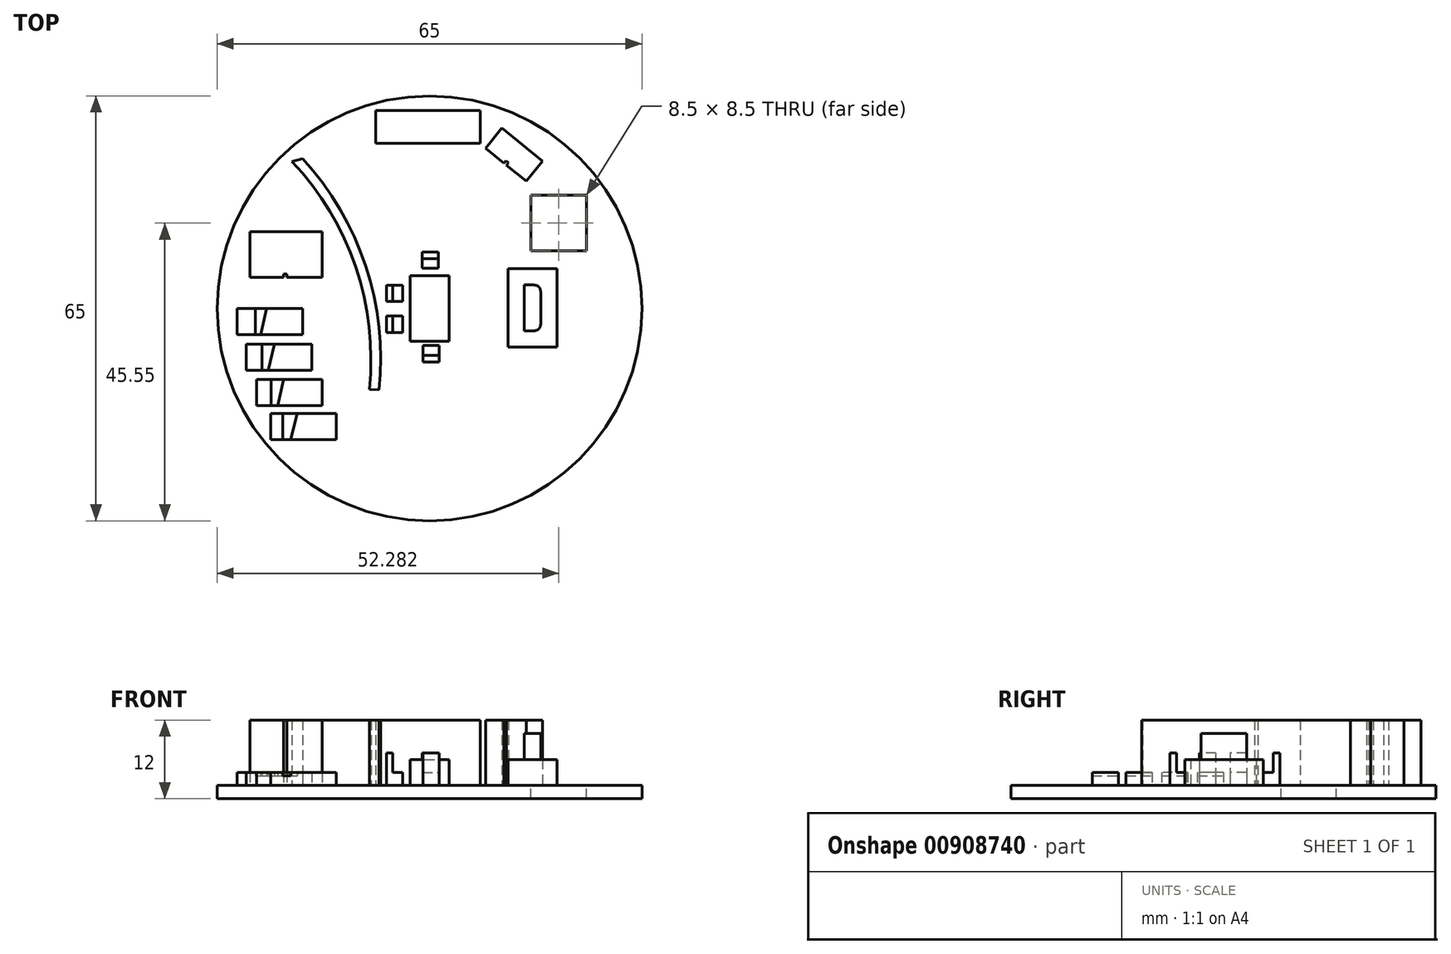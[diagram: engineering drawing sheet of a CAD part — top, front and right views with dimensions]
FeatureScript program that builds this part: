
annotation { "Feature Type Name" : "Feature", "Feature Type Description" : "" }
export const myFeature = defineFeature(function(context is Context, id is Id, definition is map)
    precondition{}
    {
        {
            var Q0;
            Q0=qCreatedBy(makeId("Top.planeOp"),FACE);
            var sketch = newSketch(context, id + "F0", { "sketchPlane" : qUnion([Q0])});
            skCircle(sketch, "E0", {"center": v(0, 0) * mm, "radius": 32.5 * mm});
            skSolve(sketch);
        }
        {
            var Q0;
            Q0=qSketchRegion(id+"F0",true);
            extrude(context, id + "F1", {"entities" : qUnion([Q0]), "depth" : 2 * mm, "offsetDistance" : 25 * mm});
        }
        {
            var Q0;
            Q0=makeQuery(id+"F1.opExtrude","CAP_FACE",FACE,{"disambiguationData":[OSD([sQuery(id+"F0.wireOp",EDGE,"E0")])],"isStart":false});
            var sketch = newSketch(context, id + "F2", { "sketchPlane" : qUnion([Q0])});
            skLineSegment(sketch, "E1.bottom", {"start": v(-8.27, 30.26) * mm, "end": v(7.73, 30.26) * mm});
            skLineSegment(sketch, "E1.top", {"start": v(-8.27, 25.26) * mm, "end": v(7.73, 25.26) * mm});
            skLineSegment(sketch, "E1.left", {"start": v(-8.27, 30.26) * mm, "end": v(-8.27, 25.26) * mm});
            skLineSegment(sketch, "E1.right", {"start": v(7.73, 30.26) * mm, "end": v(7.73, 25.26) * mm});
            skLineSegment(sketch, "E2.bottom", {"start": v(11.09, 27.6) * mm, "end": v(8.57, 24.5) * mm});
            skLineSegment(sketch, "E2.top", {"start": v(17.3, 22.56) * mm, "end": v(14.78, 19.46) * mm});
            skLineSegment(sketch, "E2.left", {"start": v(11.09, 27.6) * mm, "end": v(17.3, 22.56) * mm});
            skLineSegment(sketch, "E2.right", {"start": v(8.57, 24.5) * mm, "end": v(11.38, 22.21) * mm});
            skLineSegment(sketch, "E3.bottom", {"start": v(-27.46, 11.75) * mm, "end": v(-16.46, 11.75) * mm});
            skLineSegment(sketch, "E3.top", {"start": v(-27.46, 4.75) * mm, "end": v(-22.33, 4.75) * mm});
            skLineSegment(sketch, "E3.left", {"start": v(-27.46, 11.75) * mm, "end": v(-27.46, 4.75) * mm});
            skLineSegment(sketch, "E3.right", {"start": v(-16.46, 11.75) * mm, "end": v(-16.46, 4.75) * mm});
            skLineSegment(sketch, "E4", {"start": v(11.38, 22.21) * mm, "end": v(11.7, 22.6) * mm});
            skLineSegment(sketch, "E5", {"start": v(11.7, 22.6) * mm, "end": v(12.09, 22.28) * mm});
            skLineSegment(sketch, "E6", {"start": v(12.09, 22.28) * mm, "end": v(11.77, 21.9) * mm});
            skLineSegment(sketch, "E7.trimOffspring", {"start": v(11.77, 21.9) * mm, "end": v(14.78, 19.46) * mm});
            skArc(sketch, "E8", {"start": v(-7.72, -12.48) * mm, "mid": v(-9.77, 6.46) * mm, "end": v(-19.4, 22.9) * mm});
            skArc(sketch, "E9.0", {"start": v(-9.21, -12.36) * mm, "mid": v(-11.31, 6.36) * mm, "end": v(-21.05, 22.49) * mm});
            skLineSegment(sketch, "E10", {"start": v(-21.05, 22.49) * mm, "end": v(-19.4, 22.9) * mm});
            skLineSegment(sketch, "E11", {"start": v(-9.21, -12.36) * mm, "end": v(-7.72, -12.48) * mm});
            skLineSegment(sketch, "E12", {"start": v(-21.83, 4.75) * mm, "end": v(-21.83, 5.25) * mm});
            skLineSegment(sketch, "E13", {"start": v(-21.83, 5.25) * mm, "end": v(-22.33, 5.25) * mm});
            skLineSegment(sketch, "E14", {"start": v(-22.33, 5.25) * mm, "end": v(-22.33, 4.75) * mm});
            skLineSegment(sketch, "E15.trimOffspring", {"start": v(-21.83, 4.75) * mm, "end": v(-16.46, 4.75) * mm});
            skSolve(sketch);
        }
        {
            var Q0;
            Q0 = qSketchRegion(id + "F2", true);
            extrude(context, id + "F3", {"entities" : qUnion([Q0]), "operationType" : NewBodyOperationType.ADD, "depth" : 10 * mm, "offsetDistance" : 25 * mm});
        }
        {
            var Q0;
            Q0=makeQuery(id+"F1.opExtrude","CAP_FACE",FACE,{"disambiguationData":[OSD([sQuery(id+"F0.wireOp",EDGE,"E0")])],"isStart":false});
            var sketch = newSketch(context, id + "F4", { "sketchPlane" : qUnion([Q0])});
            skLineSegment(sketch, "E16.bottom", {"start": v(-3, 5) * mm, "end": v(3, 5) * mm});
            skLineSegment(sketch, "E16.top", {"start": v(-3, -5) * mm, "end": v(3, -5) * mm});
            skLineSegment(sketch, "E16.left", {"start": v(-3, 5) * mm, "end": v(-3, -5) * mm});
            skLineSegment(sketch, "E16.right", {"start": v(3, 5) * mm, "end": v(3, -5) * mm});
            skLineSegment(sketch, "E17.bottom", {"start": v(12, 6.08) * mm, "end": v(19.5, 6.08) * mm});
            skLineSegment(sketch, "E17.top", {"start": v(12, -5.92) * mm, "end": v(19.5, -5.92) * mm});
            skLineSegment(sketch, "E17.left", {"start": v(12, 6.08) * mm, "end": v(12, -5.92) * mm});
            skLineSegment(sketch, "E17.right", {"start": v(19.5, 6.08) * mm, "end": v(19.5, -5.92) * mm});
            skSolve(sketch);
        }
        {
            var Q0;
            Q0 = qSketchRegion(id + "F4", true);
            extrude(context, id + "F5", {"entities" : qUnion([Q0]), "operationType" : NewBodyOperationType.ADD, "depth" : 4 * mm, "offsetDistance" : 25 * mm});
        }
        {
            var Q0;
            Q0=makeQuery(id+"F5.opExtrude","CAP_FACE",FACE,{"disambiguationData":[OSD([sQuery(id+"F4.wireOp",EDGE,"E17.bottom"),sQuery(id+"F4.wireOp",EDGE,"E17.top"),sQuery(id+"F4.wireOp",EDGE,"E17.left"),sQuery(id+"F4.wireOp",EDGE,"E17.right")])],"isStart":false});
            var sketch = newSketch(context, id + "F6", { "sketchPlane" : qUnion([Q0])});
            skLineSegment(sketch, "E18.0", {"start": v(14.5, 3.58) * mm, "end": v(14.5, -3.42) * mm});
            skLineSegment(sketch, "E18.1", {"start": v(17, 3.58) * mm, "end": v(14.5, 3.58) * mm});
            skLineSegment(sketch, "E18.2", {"start": v(17, -3.42) * mm, "end": v(17, 3.58) * mm});
            skLineSegment(sketch, "E18.3", {"start": v(14.5, -3.42) * mm, "end": v(17, -3.42) * mm});
            skSolve(sketch);
        }
        {
            var Q0;
            Q0 = qSketchRegion(id + "F6", true);
            extrude(context, id + "F7", {"entities" : qUnion([Q0]), "operationType" : NewBodyOperationType.ADD, "depth" : 4 * mm, "offsetDistance" : 25 * mm});
        }
        {
            var Q0;
            Q0=makeQuery(id+"F7.opExtrude","SWEPT_EDGE",EDGE,{"disambiguationData":[OSD([sQuery(id+"F6.wireOp",EDGE,"E18.2"),sQuery(id+"F6.wireOp",EDGE,"E18.3")])]});
            var Q1;
            Q1=makeQuery(id+"F7.opExtrude","SWEPT_EDGE",EDGE,{"disambiguationData":[OSD([sQuery(id+"F6.wireOp",EDGE,"E18.1"),sQuery(id+"F6.wireOp",EDGE,"E18.2")])]});
            fillet(context, id + "F8", {"entities" : qUnion([Q0, Q1]), "radius" : 1 * mm, "tangentPropagation" : true, "allowEdgeOverflow" : false});
        }
        {
            var Q0;
            Q0=makeQuery(id+"F1.opExtrude","CAP_FACE",FACE,{"disambiguationData":[OSD([sQuery(id+"F0.wireOp",EDGE,"E0")])],"isStart":false});
            var sketch = newSketch(context, id + "F9", { "sketchPlane" : qUnion([Q0])});
            skLineSegment(sketch, "E19.bottom", {"start": v(-6.61, -1.17) * mm, "end": v(-4.11, -1.17) * mm});
            skLineSegment(sketch, "E19.top", {"start": v(-6.61, -3.67) * mm, "end": v(-4.11, -3.67) * mm});
            skLineSegment(sketch, "E19.left", {"start": v(-6.61, -1.17) * mm, "end": v(-6.61, -3.67) * mm});
            skLineSegment(sketch, "E19.right", {"start": v(-4.11, -1.17) * mm, "end": v(-4.11, -3.67) * mm});
            skLineSegment(sketch, "E20.bottom", {"start": v(-6.62, 3.55) * mm, "end": v(-4.12, 3.55) * mm});
            skLineSegment(sketch, "E20.top", {"start": v(-6.62, 1.05) * mm, "end": v(-4.12, 1.05) * mm});
            skLineSegment(sketch, "E20.left", {"start": v(-6.62, 3.55) * mm, "end": v(-6.62, 1.05) * mm});
            skLineSegment(sketch, "E20.right", {"start": v(-4.12, 3.55) * mm, "end": v(-4.12, 1.05) * mm});
            skLineSegment(sketch, "E21.bottom", {"start": v(-1.13, 8.62) * mm, "end": v(1.37, 8.62) * mm});
            skLineSegment(sketch, "E21.top", {"start": v(-1.13, 6.12) * mm, "end": v(1.37, 6.12) * mm});
            skLineSegment(sketch, "E21.left", {"start": v(-1.13, 8.62) * mm, "end": v(-1.13, 6.12) * mm});
            skLineSegment(sketch, "E21.right", {"start": v(1.37, 8.62) * mm, "end": v(1.37, 6.12) * mm});
            skLineSegment(sketch, "E22.bottom", {"start": v(-1.04, -5.68) * mm, "end": v(1.46, -5.68) * mm});
            skLineSegment(sketch, "E22.top", {"start": v(-1.04, -8.18) * mm, "end": v(1.46, -8.18) * mm});
            skLineSegment(sketch, "E22.left", {"start": v(-1.04, -5.68) * mm, "end": v(-1.04, -8.18) * mm});
            skLineSegment(sketch, "E22.right", {"start": v(1.46, -5.68) * mm, "end": v(1.46, -8.18) * mm});
            skSolve(sketch);
        }
        {
            var Q0;
            Q0 = qSketchRegion(id + "F9", true);
            extrude(context, id + "F10", {"entities" : qUnion([Q0]), "operationType" : NewBodyOperationType.ADD, "depth" : 2 * mm, "offsetDistance" : 25 * mm});
        }
        {
            var Q0;
            Q0=makeQuery(id+"F10.opExtrude","CAP_FACE",FACE,{"disambiguationData":[OSD([sQuery(id+"F9.wireOp",EDGE,"E21.bottom"),sQuery(id+"F9.wireOp",EDGE,"E21.top"),sQuery(id+"F9.wireOp",EDGE,"E21.left"),sQuery(id+"F9.wireOp",EDGE,"E21.right")])],"isStart":false});
            var sketch = newSketch(context, id + "F11", { "sketchPlane" : qUnion([Q0])});
            skLineSegment(sketch, "E23.0.0", {"start": v(-6.62, 3.55) * mm, "end": v(-6.62, 1.05) * mm});
            skLineSegment(sketch, "E23.0.1", {"start": v(-6.62, 1.05) * mm, "end": v(-4.12, 1.05) * mm});
            skLineSegment(sketch, "E23.0.2", {"start": v(-4.12, 1.05) * mm, "end": v(-4.12, 3.55) * mm});
            skLineSegment(sketch, "E23.0.3", {"start": v(-4.12, 3.55) * mm, "end": v(-6.62, 3.55) * mm});
            skLineSegment(sketch, "E24.0.0", {"start": v(-6.61, -1.17) * mm, "end": v(-6.61, -3.67) * mm});
            skLineSegment(sketch, "E24.0.1", {"start": v(-6.61, -3.67) * mm, "end": v(-4.11, -3.67) * mm});
            skLineSegment(sketch, "E24.0.2", {"start": v(-4.11, -3.67) * mm, "end": v(-4.11, -1.17) * mm});
            skLineSegment(sketch, "E24.0.3", {"start": v(-4.11, -1.17) * mm, "end": v(-6.61, -1.17) * mm});
            skLineSegment(sketch, "E25.0.0", {"start": v(-1.04, -5.68) * mm, "end": v(-1.04, -8.18) * mm});
            skLineSegment(sketch, "E25.0.1", {"start": v(-1.04, -8.18) * mm, "end": v(1.46, -8.18) * mm});
            skLineSegment(sketch, "E25.0.2", {"start": v(1.46, -8.18) * mm, "end": v(1.46, -5.68) * mm});
            skLineSegment(sketch, "E25.0.3", {"start": v(1.46, -5.68) * mm, "end": v(-1.04, -5.68) * mm});
            skLineSegment(sketch, "E26.0.0", {"start": v(-1.13, 8.62) * mm, "end": v(-1.13, 6.12) * mm});
            skLineSegment(sketch, "E26.0.1", {"start": v(-1.13, 6.12) * mm, "end": v(1.37, 6.12) * mm});
            skLineSegment(sketch, "E26.0.2", {"start": v(1.37, 6.12) * mm, "end": v(1.37, 8.62) * mm});
            skLineSegment(sketch, "E26.0.3", {"start": v(1.37, 8.62) * mm, "end": v(-1.13, 8.62) * mm});
            skLineSegment(sketch, "E27", {"start": v(-5.62, 3.55) * mm, "end": v(-5.62, 1.05) * mm});
            skPoint(sketch, "E27.endSnap0", {"position": v(-5.37, 1.05) * mm});
            skLineSegment(sketch, "E28", {"start": v(-5.61, -1.17) * mm, "end": v(-5.61, -3.67) * mm});
            skLineSegment(sketch, "E29", {"start": v(-1.13, 7.62) * mm, "end": v(1.37, 7.62) * mm});
            skLineSegment(sketch, "E30", {"start": v(-1.04, -7.18) * mm, "end": v(1.46, -7.18) * mm});
            skSolve(sketch);
        }
        {
            var Q0;
            {var subQ0=sQuery(id+"F11.wireOp",EDGE,"E25.0.1");Q0=makeQuery(id+"F11.imprint","IMPRINT",FACE,{"disambiguationData":[TD([[makeQuery(id+"F11.imprint","IMPRINT",EDGE,{"derivedFrom":subQ0}),1.0]])]});}
            var Q1;
            {var subQ0=sQuery(id+"F11.wireOp",EDGE,"E23.0.0");Q1=makeQuery(id+"F11.imprint","IMPRINT",FACE,{"disambiguationData":[TD([[makeQuery(id+"F11.imprint","IMPRINT",EDGE,{"derivedFrom":subQ0}),1.0]])]});}
            var Q2;
            {var subQ0=sQuery(id+"F11.wireOp",EDGE,"E24.0.0");Q2=makeQuery(id+"F11.imprint","IMPRINT",FACE,{"disambiguationData":[TD([[makeQuery(id+"F11.imprint","IMPRINT",EDGE,{"derivedFrom":subQ0}),1.0]])]});}
            var Q3;
            {var subQ0=sQuery(id+"F11.wireOp",EDGE,"E26.0.3");Q3=makeQuery(id+"F11.imprint","IMPRINT",FACE,{"disambiguationData":[TD([[makeQuery(id+"F11.imprint","IMPRINT",EDGE,{"derivedFrom":subQ0}),-1.0]])]});}
            extrude(context, id + "F12", {"entities" : qUnion([Q0, Q1, Q2, Q3]), "operationType" : NewBodyOperationType.ADD, "depth" : 3 * mm, "offsetDistance" : 25 * mm});
        }
        {
            var Q0;
            Q0=makeQuery(id+"F1.opExtrude","CAP_FACE",FACE,{"disambiguationData":[OSD([sQuery(id+"F0.wireOp",EDGE,"E0")])],"isStart":false});
            var sketch = newSketch(context, id + "F13", { "sketchPlane" : qUnion([Q0])});
            skLineSegment(sketch, "E31.bottom", {"start": v(15.53, 17.3) * mm, "end": v(24.03, 17.3) * mm});
            skLineSegment(sketch, "E31.top", {"start": v(15.53, 8.8) * mm, "end": v(24.03, 8.8) * mm});
            skLineSegment(sketch, "E31.left", {"start": v(15.53, 17.3) * mm, "end": v(15.53, 8.8) * mm});
            skLineSegment(sketch, "E31.right", {"start": v(24.03, 17.3) * mm, "end": v(24.03, 8.8) * mm});
            skSolve(sketch);
        }
        {
            var Q0;
            Q0 = qSketchRegion(id + "F13", true);
            extrude(context, id + "F14", {"entities" : qUnion([Q0]), "operationType" : NewBodyOperationType.REMOVE, "oppositeDirection" : true, "depth" : 25 * mm, "offsetDistance" : 25 * mm});
        }
        {
            var Q0;
            Q0=makeQuery(id+"F1.opExtrude","CAP_FACE",FACE,{"disambiguationData":[OSD([sQuery(id+"F0.wireOp",EDGE,"E0")])],"isStart":false});
            var sketch = newSketch(context, id + "F15", { "sketchPlane" : qUnion([Q0])});
            skLineSegment(sketch, "E32.bottom", {"start": v(-29.43, 0) * mm, "end": v(-19.43, 0) * mm});
            skLineSegment(sketch, "E32.top", {"start": v(-29.43, -4) * mm, "end": v(-19.43, -4) * mm});
            skLineSegment(sketch, "E32.left", {"start": v(-29.43, 0) * mm, "end": v(-29.43, -4) * mm});
            skLineSegment(sketch, "E32.right", {"start": v(-19.43, 0) * mm, "end": v(-19.43, -4) * mm});
            skLineSegment(sketch, "E33.bottom", {"start": v(-28.04, -5.48) * mm, "end": v(-18.04, -5.48) * mm});
            skLineSegment(sketch, "E33.top", {"start": v(-28.04, -9.48) * mm, "end": v(-18.04, -9.48) * mm});
            skLineSegment(sketch, "E33.left", {"start": v(-28.04, -5.48) * mm, "end": v(-28.04, -9.48) * mm});
            skLineSegment(sketch, "E33.right", {"start": v(-18.04, -5.48) * mm, "end": v(-18.04, -9.48) * mm});
            skLineSegment(sketch, "E34.bottom", {"start": v(-26.46, -10.89) * mm, "end": v(-16.46, -10.89) * mm});
            skLineSegment(sketch, "E34.top", {"start": v(-26.46, -14.89) * mm, "end": v(-16.46, -14.89) * mm});
            skLineSegment(sketch, "E34.left", {"start": v(-26.46, -10.89) * mm, "end": v(-26.46, -14.89) * mm});
            skLineSegment(sketch, "E34.right", {"start": v(-16.46, -10.89) * mm, "end": v(-16.46, -14.89) * mm});
            skLineSegment(sketch, "E35.bottom", {"start": v(-24.28, -16.09) * mm, "end": v(-14.28, -16.09) * mm});
            skLineSegment(sketch, "E35.top", {"start": v(-24.28, -20.09) * mm, "end": v(-14.28, -20.09) * mm});
            skLineSegment(sketch, "E35.left", {"start": v(-24.28, -16.09) * mm, "end": v(-24.28, -20.09) * mm});
            skLineSegment(sketch, "E35.right", {"start": v(-14.28, -16.09) * mm, "end": v(-14.28, -20.09) * mm});
            skSolve(sketch);
        }
        {
            var Q0;
            Q0 = qSketchRegion(id + "F15", true);
            extrude(context, id + "F16", {"entities" : qUnion([Q0]), "operationType" : NewBodyOperationType.ADD, "depth" : 1.5 * mm, "offsetDistance" : 25 * mm});
        }
        {
            var Q0;
            Q0=makeQuery(id+"F16.opExtrude","CAP_FACE",FACE,{"disambiguationData":[OSD([sQuery(id+"F15.wireOp",EDGE,"E32.bottom"),sQuery(id+"F15.wireOp",EDGE,"E32.top"),sQuery(id+"F15.wireOp",EDGE,"E32.left"),sQuery(id+"F15.wireOp",EDGE,"E32.right")])],"isStart":false});
            var sketch = newSketch(context, id + "F17", { "sketchPlane" : qUnion([Q0])});
            skLineSegment(sketch, "E36.0.0", {"start": v(-29.43, 0) * mm, "end": v(-29.43, -4) * mm});
            skLineSegment(sketch, "E36.0.1", {"start": v(-29.43, -4) * mm, "end": v(-26.64, -4) * mm});
            skLineSegment(sketch, "E36.0.2", {"start": v(-19.43, -4) * mm, "end": v(-19.43, 0) * mm});
            skLineSegment(sketch, "E36.0.3", {"start": v(-19.43, 0) * mm, "end": v(-24.93, 0) * mm});
            skLineSegment(sketch, "E37.0.0", {"start": v(-28.04, -5.48) * mm, "end": v(-28.04, -9.48) * mm});
            skLineSegment(sketch, "E37.0.1", {"start": v(-28.04, -9.48) * mm, "end": v(-25.64, -9.48) * mm});
            skLineSegment(sketch, "E37.0.2", {"start": v(-18.04, -9.48) * mm, "end": v(-18.04, -5.48) * mm});
            skLineSegment(sketch, "E37.0.3", {"start": v(-18.04, -5.48) * mm, "end": v(-23.74, -5.48) * mm});
            skLineSegment(sketch, "E38.0.0", {"start": v(-26.46, -10.89) * mm, "end": v(-26.46, -14.89) * mm});
            skLineSegment(sketch, "E38.0.1", {"start": v(-26.46, -14.89) * mm, "end": v(-24.26, -14.89) * mm});
            skLineSegment(sketch, "E38.0.2", {"start": v(-16.46, -14.89) * mm, "end": v(-16.46, -10.89) * mm});
            skLineSegment(sketch, "E38.0.3", {"start": v(-16.46, -10.89) * mm, "end": v(-22.35, -10.89) * mm});
            skLineSegment(sketch, "E39.0.0", {"start": v(-24.28, -16.09) * mm, "end": v(-24.28, -20.09) * mm});
            skLineSegment(sketch, "E39.0.1", {"start": v(-24.28, -20.09) * mm, "end": v(-22.48, -20.09) * mm});
            skLineSegment(sketch, "E39.0.2", {"start": v(-14.28, -20.09) * mm, "end": v(-14.28, -16.09) * mm});
            skLineSegment(sketch, "E39.0.3", {"start": v(-14.28, -16.09) * mm, "end": v(-20.26, -16.09) * mm});
            skLineSegment(sketch, "E40.top", {"start": v(-26.64, -4) * mm, "end": v(-25.81, -4) * mm});
            skLineSegment(sketch, "E40.left", {"start": v(-26.64, 0) * mm, "end": v(-26.64, -4) * mm});
            skLineSegment(sketch, "E41.top", {"start": v(-25.64, -9.48) * mm, "end": v(-24.7, -9.48) * mm});
            skLineSegment(sketch, "E41.left", {"start": v(-25.64, -5.48) * mm, "end": v(-25.64, -9.48) * mm});
            skLineSegment(sketch, "E42.top", {"start": v(-24.26, -14.89) * mm, "end": v(-23.25, -14.89) * mm});
            skLineSegment(sketch, "E42.left", {"start": v(-24.26, -10.89) * mm, "end": v(-24.26, -14.89) * mm});
            skLineSegment(sketch, "E43.bottom", {"start": v(-22.48, -16.09) * mm, "end": v(-20.26, -16.09) * mm});
            skLineSegment(sketch, "E43.left", {"start": v(-22.48, -16.09) * mm, "end": v(-22.48, -20.09) * mm});
            skLineSegment(sketch, "E44", {"start": v(-25.81, -4) * mm, "end": v(-24.93, 0) * mm});
            skLineSegment(sketch, "E45", {"start": v(-24.7, -9.48) * mm, "end": v(-23.74, -5.48) * mm});
            skLineSegment(sketch, "E46", {"start": v(-23.25, -14.89) * mm, "end": v(-22.35, -10.89) * mm});
            skLineSegment(sketch, "E47", {"start": v(-21.28, -20.09) * mm, "end": v(-20.26, -16.09) * mm});
            skLineSegment(sketch, "E48.trimOffspring", {"start": v(-26.64, 0) * mm, "end": v(-29.43, 0) * mm});
            skLineSegment(sketch, "E49.trimOffspring", {"start": v(-25.81, -4) * mm, "end": v(-19.43, -4) * mm});
            skLineSegment(sketch, "E50.trimOffspring", {"start": v(-25.64, -5.48) * mm, "end": v(-28.04, -5.48) * mm});
            skLineSegment(sketch, "E51.trimOffspring", {"start": v(-24.7, -9.48) * mm, "end": v(-18.04, -9.48) * mm});
            skLineSegment(sketch, "E52.trimOffspring", {"start": v(-24.26, -10.89) * mm, "end": v(-26.46, -10.89) * mm});
            skLineSegment(sketch, "E53.trimOffspring", {"start": v(-23.25, -14.89) * mm, "end": v(-16.46, -14.89) * mm});
            skLineSegment(sketch, "E54.trimOffspring", {"start": v(-22.48, -16.09) * mm, "end": v(-24.28, -16.09) * mm});
            skLineSegment(sketch, "E55.trimOffspring", {"start": v(-21.28, -20.09) * mm, "end": v(-14.28, -20.09) * mm});
            skSolve(sketch);
        }
        {
            var Q0;
            Q0 = qSketchRegion(id + "F17", true);
            extrude(context, id + "F18", {"entities" : qUnion([Q0]), "operationType" : NewBodyOperationType.ADD, "depth" : 0.5 * mm, "offsetDistance" : 25 * mm});
        }
    });
